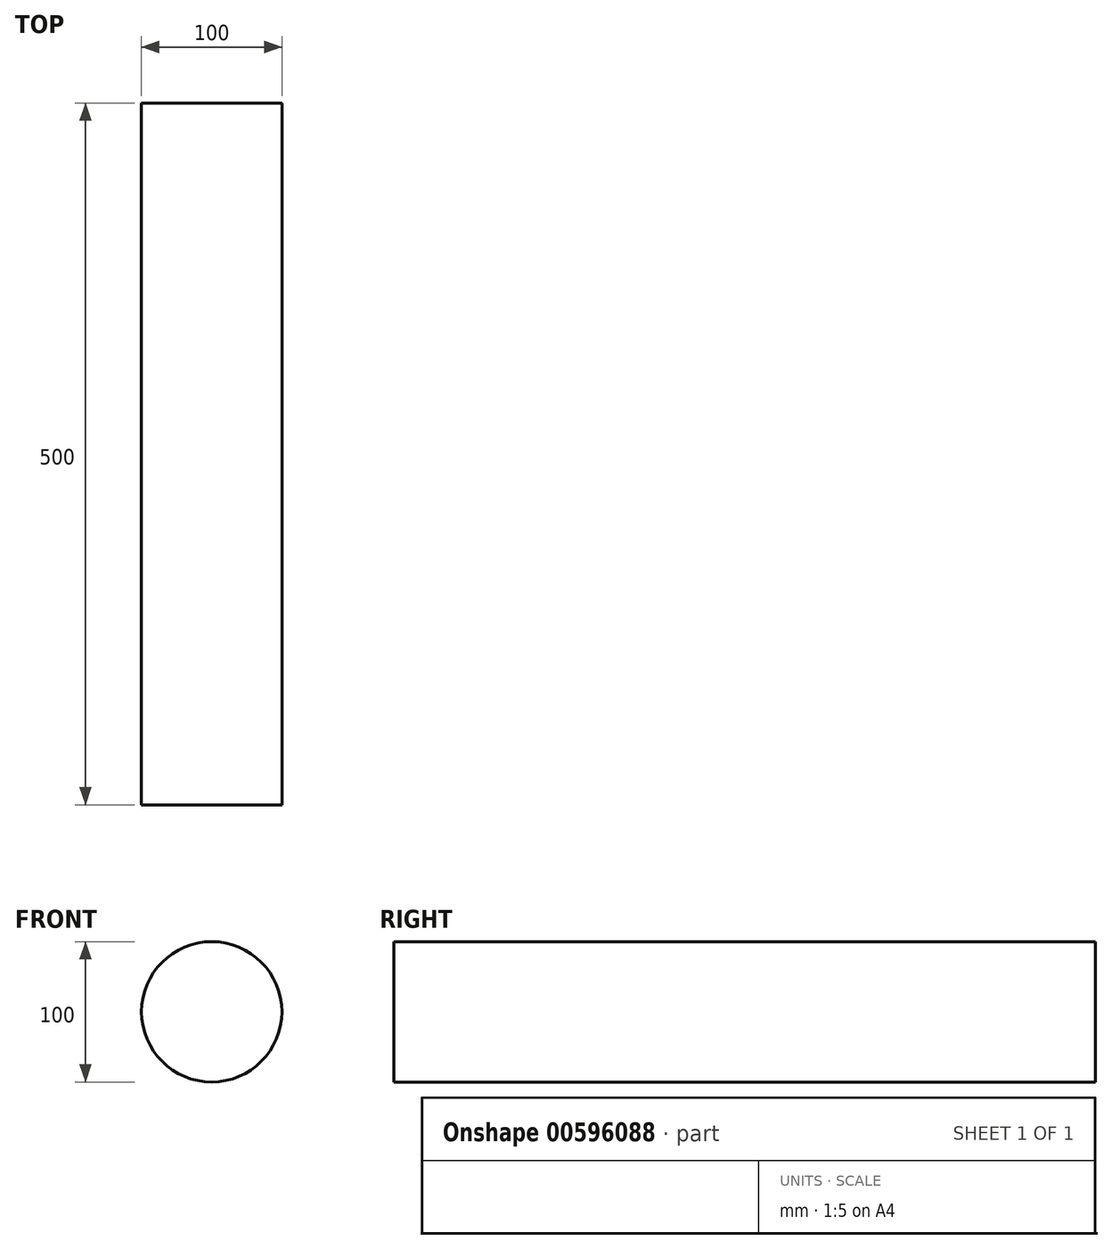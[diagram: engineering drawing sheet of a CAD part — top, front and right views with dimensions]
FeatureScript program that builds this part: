
annotation { "Feature Type Name" : "Feature", "Feature Type Description" : "" }
export const myFeature = defineFeature(function(context is Context, id is Id, definition is map)
    precondition{}
    {
        {
            var Q0;
            Q0=qCreatedBy(makeId("Front.planeOp"),FACE);
            var sketch = newSketch(context, id + "F0", { "sketchPlane" : qUnion([Q0])});
            skCircle(sketch, "E0", {"center": v(0, 0) * mm, "radius": 50 * mm});
            skSolve(sketch);
        }
        {
            var Q0;
            Q0 = qSketchRegion(id + "F0", true);
            extrude(context, id + "F1", {"entities" : qUnion([Q0]), "endBound" : BoundingType.SYMMETRIC, "depth" : 500 * mm, "offsetDistance" : 25 * mm});
        }
    });
